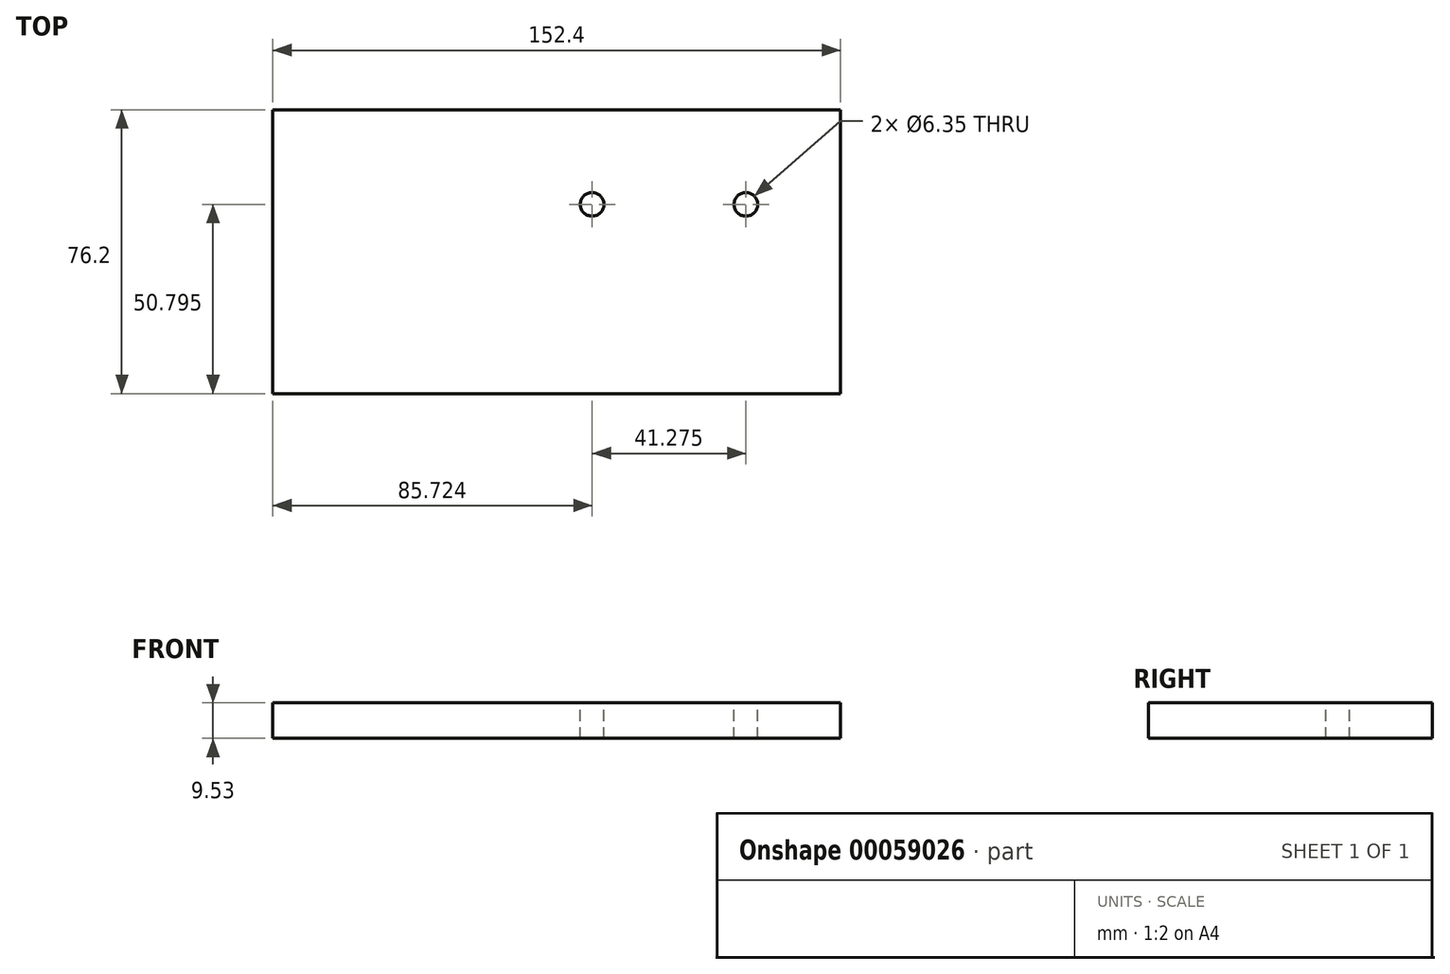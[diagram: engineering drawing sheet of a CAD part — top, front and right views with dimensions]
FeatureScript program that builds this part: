
annotation { "Feature Type Name" : "Feature", "Feature Type Description" : "" }
export const myFeature = defineFeature(function(context is Context, id is Id, definition is map)
    precondition{}
    {
        {
            var Q0;
            Q0=qCreatedBy(makeId("Top.planeOp"),FACE);
            var sketch = newSketch(context, id + "F0", { "sketchPlane" : qUnion([Q0])});
            skLineSegment(sketch, "E0.bottom", {"start": v(-148.5, -2.73) * mm, "end": v(3.9, -2.73) * mm});
            skLineSegment(sketch, "E0.top", {"start": v(-148.5, -78.93) * mm, "end": v(3.9, -78.93) * mm});
            skLineSegment(sketch, "E0.left", {"start": v(-148.5, -2.73) * mm, "end": v(-148.5, -78.93) * mm});
            skLineSegment(sketch, "E0.right", {"start": v(3.9, -2.73) * mm, "end": v(3.9, -78.93) * mm});
            skSolve(sketch);
        }
        {
            var Q0;
            Q0=qSketchRegion(id+"F0",true);
            extrude(context, id + "F1", {"entities" : qUnion([Q0]), "depth" : 9.52 * mm});
        }
        {
            var Q0;
            Q0=makeQuery(id+"F1.opExtrude","CAP_FACE",FACE,{"disambiguationData":[OSD([sQuery(id+"F0.wireOp",EDGE,"E0.bottom"),sQuery(id+"F0.wireOp",EDGE,"E0.top"),sQuery(id+"F0.wireOp",EDGE,"E0.left"),sQuery(id+"F0.wireOp",EDGE,"E0.right")])],"isStart":false});
            var sketch = newSketch(context, id + "F2", { "sketchPlane" : qUnion([Q0])});
            skCircle(sketch, "E1", {"center": v(-21.5, -28.13) * mm, "radius": 3.17 * mm});
            skSolve(sketch);
        }
        {
            var Q0;
            Q0=qSketchRegion(id+"F2",true);
            extrude(context, id + "F3", {"entities" : qUnion([Q0]), "operationType" : NewBodyOperationType.REMOVE, "oppositeDirection" : true, "depth" : 25.4 * mm});
        }
        {
            var Q0;
            Q0=makeQuery(id+"F1.opExtrude","CAP_FACE",FACE,{"disambiguationData":[OSD([sQuery(id+"F0.wireOp",EDGE,"E0.bottom"),sQuery(id+"F0.wireOp",EDGE,"E0.top"),sQuery(id+"F0.wireOp",EDGE,"E0.left"),sQuery(id+"F0.wireOp",EDGE,"E0.right")])],"isStart":false});
            var sketch = newSketch(context, id + "F4", { "sketchPlane" : qUnion([Q0])});
            skCircle(sketch, "E2", {"center": v(-62.77, -28.13) * mm, "radius": 3.18 * mm});
            skSolve(sketch);
        }
        {
            var Q0;
            Q0=qSketchRegion(id+"F4",true);
            extrude(context, id + "F5", {"entities" : qUnion([Q0]), "operationType" : NewBodyOperationType.REMOVE, "oppositeDirection" : true, "depth" : 25.4 * mm});
        }
    });
